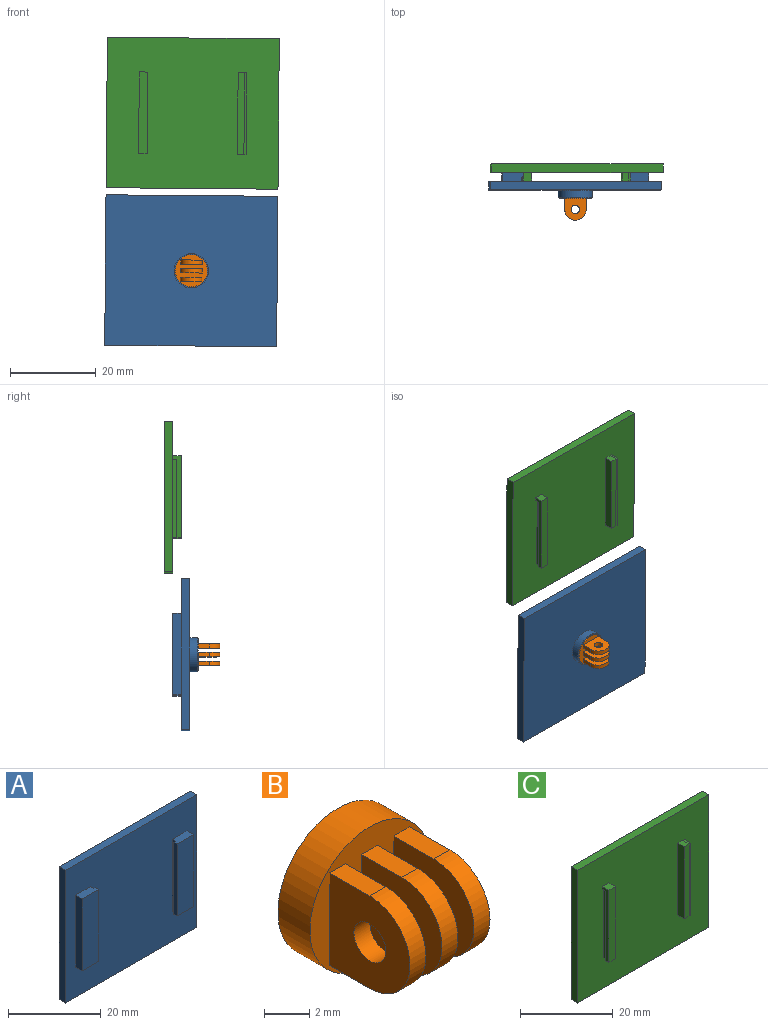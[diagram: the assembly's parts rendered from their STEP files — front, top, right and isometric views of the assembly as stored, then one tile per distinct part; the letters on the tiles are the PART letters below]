
ASSEMBLY  parts=3 mates=2
PART A: 24 faces, bbox 40x5.8x35 mm
  f0: plane 40x2mm, normal (0,0,-1), area 80mm2, adj f1,f3,f4,f5
  f1: plane 35x2mm, normal (1,0,0), area 70mm2, adj f0,f2,f4,f5
  f2: plane 40x2mm, normal (0,0,1), area 80mm2, adj f1,f3,f4,f5
  f3: plane 35x2mm, normal (-1,0,0), area 70mm2, adj f0,f2,f4,f5
  f4: plane 40x35mm, normal (0,1,0), area 1349.7mm2, adj f0,f1,f2,f3,f21
  f5: plane 40x35mm, normal (0,-1,0), area 1229mm2, adj f0,f1,f2,f3,f6,f7,f8,f10
  f6: plane 5x2mm, normal (0,0,1), area 9.5mm2, adj f5,f8,f9,f16,f17,f18
  f7: plane 5x2mm, normal (0,0,-1), area 9.5mm2, adj f5,f8,f9,f16,f17,f18
  f8: plane 19x2mm, normal (1,0,0), area 38mm2, adj f5,f6,f7,f9
  f9: plane 19x5mm, normal (0,-1,0), area 95mm2, adj f6,f7,f8,f17
  f10: plane 5x2mm, normal (0,0,1), area 9.5mm2, adj f5,f11,f13,f14,f15,f19
  f11: plane 19x2mm, normal (-1,0,0), area 38mm2, adj f5,f10,f12,f13
  f12: plane 5x2mm, normal (0,0,-1), area 9.5mm2, adj f5,f11,f13,f14,f15,f19
  f13: plane 19x5mm, normal (0,-1,0), area 95mm2, adj f10,f11,f12,f15
  f14: plane 19x0.5mm, normal (0,1,0), area 9.5mm2, adj f10,f12,f15,f19
  f15: plane 19x1mm, normal (1,0,0), area 19mm2, adj f10,f12,f13,f14
  f16: plane 19x0.5mm, normal (0,1,0), area 9.5mm2, adj f6,f7,f17,f18
  f17: plane 19x1mm, normal (-1,0,0), area 19mm2, adj f6,f7,f9,f16
  f18: plane 19x1mm, normal (-1,0,0), area 19mm2, adj f5,f6,f7,f16
  f19: plane 19x1mm, normal (1,0,0), area 19mm2, adj f5,f10,f12,f14
  f20: cylinder r=3.75mm len=7.5mm, axis (0,-1,0), area 42.4mm2, adj f22,f23
  f21: cylinder r=4mm len=8mm, axis (0,-1,0), area 45.2mm2, adj f4,f22
  f22: plane 8x8mm, normal (0,1,0), area 6.1mm2, adj f20,f21
  f23: plane 7.5x7.5mm, normal (0,1,0), area 44.2mm2, adj f20
PART B: 21 faces, bbox 7.5x7x7.5 mm
  f0: plane 7.5x7.5mm, normal (0,-1,0), area 29.2mm2, adj f1,f3,f4,f5,f6,f7,f8,f9
  f1: cylinder r=3.75mm len=7.5mm, axis (0,1,0), area 47.1mm2, adj f0,f2
  f2: plane 7.5x7.5mm, normal (0,1,0), area 44.2mm2, adj f1
  f3: plane 2.5x1mm, normal (0,0,1), area 2.5mm2, adj f0,f4,f6,f17
  f4: plane 5x5mm, normal (-1,0,0), area 19.2mm2, adj f0,f3,f5,f17,f20
  f5: plane 2.5x1mm, normal (0,0,-1), area 2.5mm2, adj f0,f4,f6,f17
  f6: plane 5x5mm, normal (1,0,0), area 19.2mm2, adj f0,f3,f5,f17,f20
  f7: plane 5x5mm, normal (-1,0,0), area 19.2mm2, adj f0,f8,f10,f15,f19
  f8: plane 2.5x1mm, normal (0,0,-1), area 2.5mm2, adj f0,f7,f9,f15
  f9: plane 5x5mm, normal (1,0,0), area 19.2mm2, adj f0,f8,f10,f15,f19
  f10: plane 2.5x1mm, normal (0,0,1), area 2.5mm2, adj f0,f7,f9,f15
  f11: plane 5x5mm, normal (-1,0,0), area 19.2mm2, adj f0,f12,f14,f16,f18
  f12: plane 2.5x1mm, normal (0,0,-1), area 2.5mm2, adj f0,f11,f13,f16
  f13: plane 5x5mm, normal (1,0,0), area 19.2mm2, adj f0,f12,f14,f16,f18
  f14: plane 2.5x1mm, normal (0,0,1), area 2.5mm2, adj f0,f11,f13,f16
  f15: cylinder r=2.5mm len=5mm, axis (1,0,0), area 7.9mm2, adj f7,f8,f9,f10
  f16: cylinder r=2.5mm len=5mm, axis (1,0,0), area 7.9mm2, adj f11,f12,f13,f14
  f17: cylinder r=2.5mm len=5mm, axis (1,0,0), area 7.9mm2, adj f3,f4,f5,f6
  f18: cylinder r=1mm len=2mm, axis (-1,0,0), area 6.3mm2, adj f11,f13
  f19: cylinder r=1mm len=2mm, axis (-1,0,0), area 6.3mm2, adj f7,f9
  f20: cylinder r=1mm len=2mm, axis (-1,0,0), area 6.3mm2, adj f4,f6
PART C: 25 faces, bbox 40x4x35 mm
  f0: plane 40x35mm, normal (0,-1,0), area 1342mm2, adj f1,f2,f3,f4,f6,f7,f8,f9
  f1: plane 35x2mm, normal (-1,0,0), area 70mm2, adj f0,f2,f4,f5
  f2: plane 40x2mm, normal (0,0,-1), area 80mm2, adj f0,f1,f3,f5
  f3: plane 35x2mm, normal (1,0,0), area 70mm2, adj f0,f2,f4,f5
  f4: plane 40x2mm, normal (0,0,1), area 80mm2, adj f0,f1,f3,f5
  f5: plane 40x35mm, normal (0,1,0), area 1400mm2, adj f1,f2,f3,f4
  f6: plane 17.78x1mm, normal (1,0,0), area 17.8mm2, adj f0,f9,f17,f18
  f7: plane 2x1.5mm, normal (0,0,1), area 3mm2, adj f0,f8,f10,f19
  f8: plane 19x2mm, normal (-1,0,0), area 38mm2, adj f0,f7,f9,f10
  f9: plane 2x1.5mm, normal (0,0,-1), area 3mm2, adj f0,f6,f8,f10,f16
  f10: plane 19x1.5mm, normal (0,-1,0), area 28.5mm2, adj f7,f8,f9,f20
  f11: plane 18.29x1mm, normal (-1,0,0), area 18.3mm2, adj f0,f12,f22,f23
  f12: plane 2x2mm, normal (0,0,-1), area 3.5mm2, adj f0,f11,f13,f15,f23,f24
  f13: plane 19x2mm, normal (1,0,0), area 38mm2, adj f0,f12,f14,f15
  f14: plane 2x2mm, normal (0,0,1), area 4mm2, adj f0,f13,f15,f24
  f15: plane 19x2mm, normal (0,-1,0), area 38mm2, adj f12,f13,f14,f24
  f16: plane 1.05x0.5mm, normal (-0.05,0,-1), area 0.5mm2, adj f9,f17,f20,f21
  f17: plane 17.8x0.5mm, normal (-0.05,1,0), area 8.9mm2, adj f6,f16,f18,f21
  f18: plane 1x0.5mm, normal (-0.05,0,-1), area 0.5mm2, adj f0,f6,f17,f21
  f19: plane 2.03x0.5mm, normal (-0.05,0,1), area 1mm2, adj f0,f7,f20,f21
  f20: plane 19.05x0.5mm, normal (-0.05,-1,0), area 9.5mm2, adj f10,f16,f19,f21
  f21: plane 19.05x2.03mm, normal (1,0,0), area 21.3mm2, adj f0,f16,f17,f18,f19,f20
  f22: plane 1x0.5mm, normal (0,0,-1), area 0.5mm2, adj f0,f11,f23,f24
  f23: plane 18.29x0.5mm, normal (0,1,0), area 9.1mm2, adj f11,f12,f22,f24
  f24: plane 19x2mm, normal (-1,0,0), area 19.7mm2, adj f0,f12,f14,f15,f22,f23
PLACE A rot(axis=(1,0,0),180deg) t=(46.09,53.82,10.65)mm fixed
PLACE B rot(axis=(0,1,0),90.7deg) t=(46.09,51.82,10.65)mm
PLACE C rot(axis=(0,1,0),0.5deg) t=(46.41,55.82,47.3)mm
MATE slider A.f10 <-> C.f12  axis (-0.01,0,-1) through (34.01,55.32,1.26)mm
MATE revolute A.f20 <-> B.f1  axis (0,-1,0) through (46.09,51.82,10.65)mm
